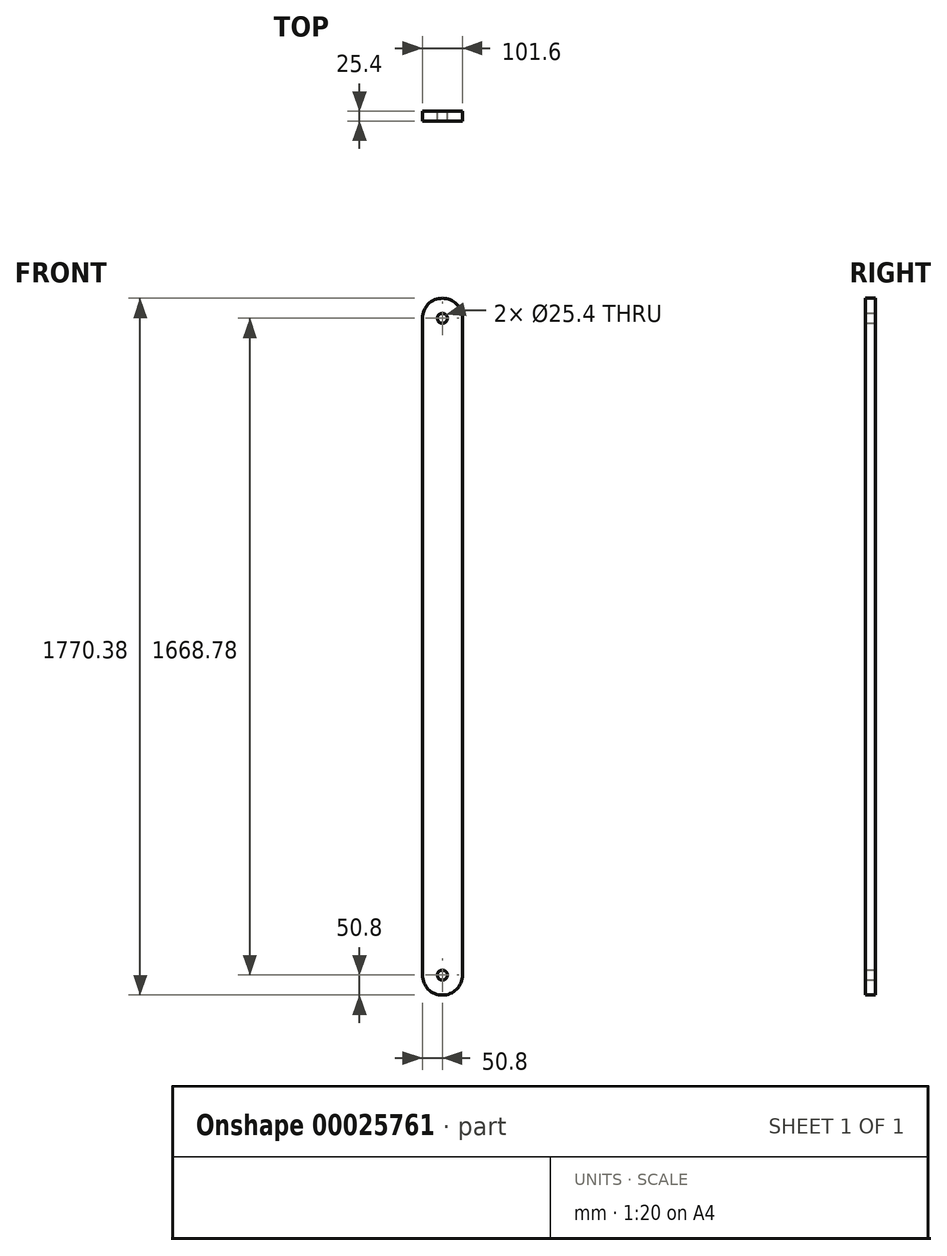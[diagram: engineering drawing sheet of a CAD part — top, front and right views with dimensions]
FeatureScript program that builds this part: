
annotation { "Feature Type Name" : "Feature", "Feature Type Description" : "" }
export const myFeature = defineFeature(function(context is Context, id is Id, definition is map)
    precondition{}
    {
        {
            var Q0;
            Q0=qCreatedBy(makeId("Front.planeOp"),FACE);
            var sketch = newSketch(context, id + "F0", { "sketchPlane" : qUnion([Q0])});
            skCircle(sketch, "E0", {"center": v(0, 0) * mm, "radius": 12.7 * mm});
            skLineSegment(sketch, "E1", {"start": v(50.8, 0) * mm, "end": v(50.8, 1668.78) * mm});
            skLineSegment(sketch, "E2", {"start": v(-50.8, 0) * mm, "end": v(-50.8, 1668.78) * mm});
            skArc(sketch, "E3", {"start": v(-50.8, 0) * mm, "mid": v(0, -50.8) * mm, "end": v(50.8, 0) * mm});
            skArc(sketch, "E4", {"start": v(50.8, 1668.78) * mm, "mid": v(0, 1719.58) * mm, "end": v(-50.8, 1668.78) * mm});
            skCircle(sketch, "E5", {"center": v(0, 1668.78) * mm, "radius": 12.7 * mm});
            skSolve(sketch);
        }
        {
            var Q0;
            Q0=qSketchRegion(id+"F0",true);
            extrude(context, id + "F1", {"entities" : qUnion([Q0]), "depth" : 25.4 * mm});
        }
    });
